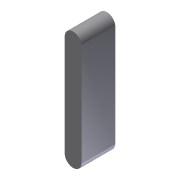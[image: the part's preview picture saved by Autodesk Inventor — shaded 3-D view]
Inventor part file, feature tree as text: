
AUTODESK INVENTOR PART (.ipt)
format: ipt  version: 2012 (Build 160160000, 160)  size: 71,168 bytes
history: native  units: in
note: dims shown in document units (in); Inventor stores cm internally (conversion verified against a paired STEP export)
features: extrude x1, sketch x1
ambient origin geometry x8: Origin, YZ Plane, XZ Plane, XY Plane, X Axis, Y Axis, Z Axis, Center Point
bodies: Solid1 (feature_tree)
feature tree (2):
  extrude  "Extrusion1"  Depth=12.0in
  sketch  "Sketch1"  dims[d0=1.0in d1=12.0in d2=4.0in d3=0.0in]
